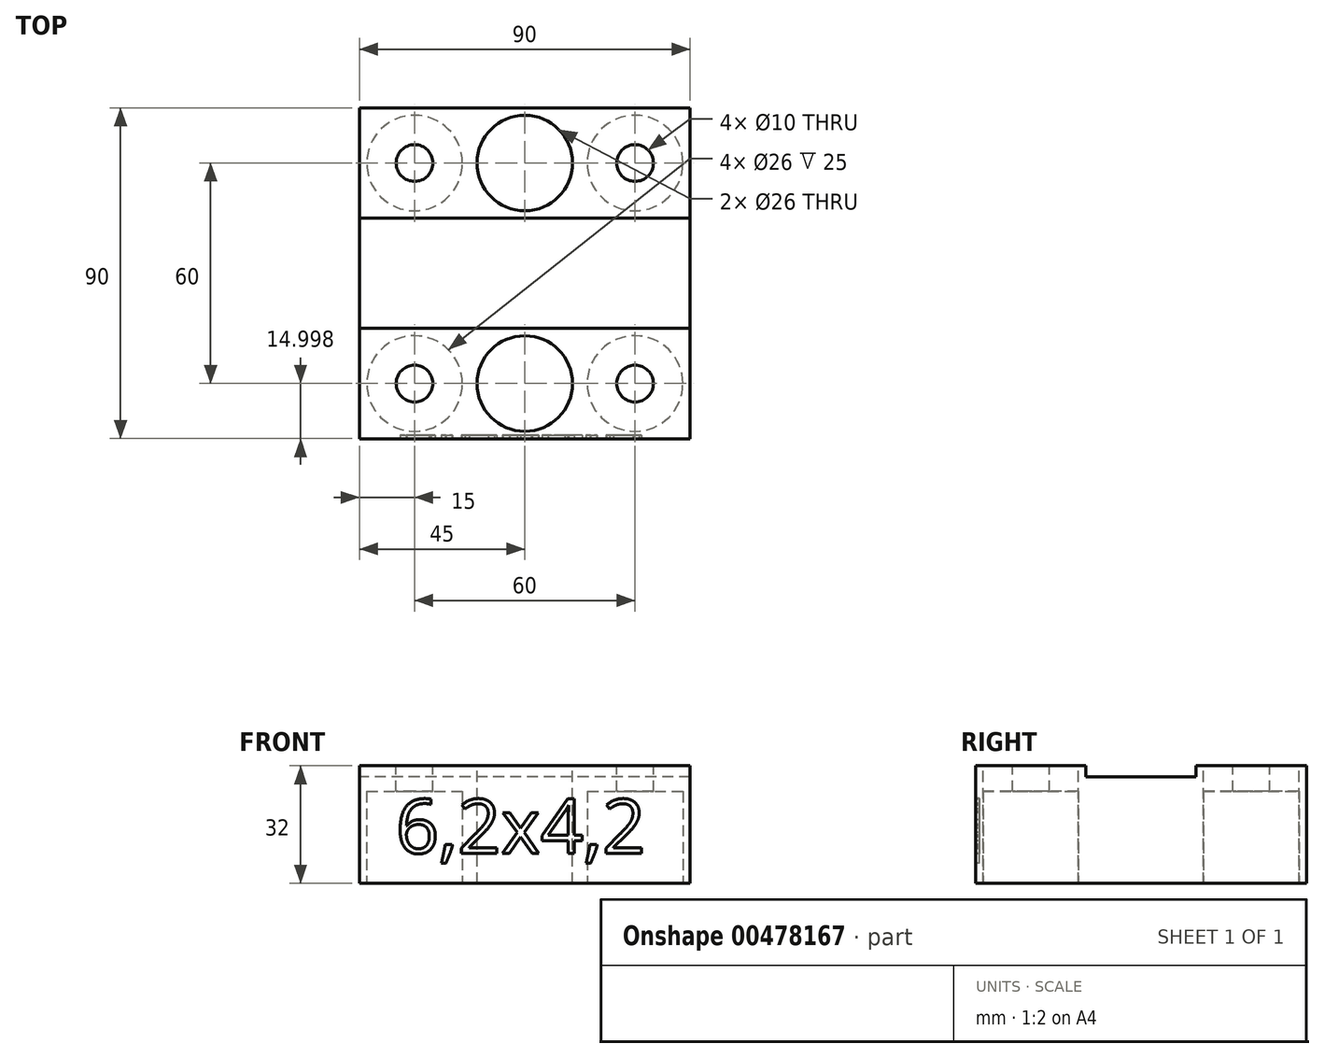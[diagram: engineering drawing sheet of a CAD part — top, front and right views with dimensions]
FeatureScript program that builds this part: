
annotation { "Feature Type Name" : "Feature", "Feature Type Description" : "" }
export const myFeature = defineFeature(function(context is Context, id is Id, definition is map)
    precondition{}
    {
        {
            var Q0;
            Q0=qCreatedBy(makeId("Right.planeOp"),FACE);
            var sketch = newSketch(context, id + "F0", { "sketchPlane" : qUnion([Q0])});
            skLineSegment(sketch, "E0", {"start": v(-46.9, -19.75) * mm, "end": v(43.1, -19.75) * mm});
            skLineSegment(sketch, "E1", {"start": v(43.1, -19.75) * mm, "end": v(43.1, 12.25) * mm});
            skLineSegment(sketch, "E2", {"start": v(43.1, 12.25) * mm, "end": v(13.1, 12.25) * mm});
            skLineSegment(sketch, "E3", {"start": v(13.1, 12.25) * mm, "end": v(13.1, 9.25) * mm});
            skLineSegment(sketch, "E4", {"start": v(13.1, 9.25) * mm, "end": v(-16.9, 9.25) * mm});
            skLineSegment(sketch, "E5", {"start": v(-16.9, 9.25) * mm, "end": v(-16.9, 12.25) * mm});
            skLineSegment(sketch, "E6", {"start": v(-16.9, 12.25) * mm, "end": v(-46.9, 12.25) * mm});
            skLineSegment(sketch, "E7", {"start": v(-46.9, 12.25) * mm, "end": v(-46.9, -19.75) * mm});
            skSolve(sketch);
        }
        {
            var Q0;
            Q0 = qSketchRegion(id + "F0", true);
            extrude(context, id + "F1", {"entities" : qUnion([Q0]), "depth" : 90 * mm});
        }
        {
            var Q0;
            Q0=makeQuery(id+"F1.opExtrude","SWEPT_FACE",FACE,{"disambiguationData":[OSD([sQuery(id+"F0.wireOp",EDGE,"E2")])]});
            var sketch = newSketch(context, id + "F2", { "sketchPlane" : qUnion([Q0])});
            skCircle(sketch, "E8", {"center": v(15, 28.1) * mm, "radius": 5 * mm});
            skCircle(sketch, "E9", {"center": v(75, 28.1) * mm, "radius": 5 * mm});
            skCircle(sketch, "E10", {"center": v(15, -31.9) * mm, "radius": 5 * mm});
            skCircle(sketch, "E11", {"center": v(75, -31.9) * mm, "radius": 5 * mm});
            skCircle(sketch, "E12", {"center": v(45, 28.1) * mm, "radius": 13 * mm});
            skCircle(sketch, "E13", {"center": v(45, -31.9) * mm, "radius": 13 * mm});
            skSolve(sketch);
        }
        {
            var Q0;
            Q0 = qSketchRegion(id + "F2", true);
            extrude(context, id + "F3", {"entities" : qUnion([Q0]), "operationType" : NewBodyOperationType.REMOVE, "endBound" : BoundingType.UP_TO_NEXT, "oppositeDirection" : true, "depth" : 25 * mm});
        }
        {
            var Q0;
            Q0=makeQuery(id+"F1.opExtrude","SWEPT_FACE",FACE,{"disambiguationData":[OSD([sQuery(id+"F0.wireOp",EDGE,"E0")])]});
            var sketch = newSketch(context, id + "F4", { "sketchPlane" : qUnion([Q0])});
            skCircle(sketch, "E14", {"center": v(15, 31.9) * mm, "radius": 13 * mm});
            skCircle(sketch, "E15", {"center": v(75, 31.9) * mm, "radius": 13 * mm});
            skCircle(sketch, "E16", {"center": v(15, -28.1) * mm, "radius": 13 * mm});
            skCircle(sketch, "E17", {"center": v(75, -28.1) * mm, "radius": 13 * mm});
            skSolve(sketch);
        }
        {
            var Q0;
            Q0 = qSketchRegion(id + "F4", true);
            extrude(context, id + "F5", {"entities" : qUnion([Q0]), "operationType" : NewBodyOperationType.REMOVE, "oppositeDirection" : true, "depth" : 25 * mm});
        }
        {
            var Q0;
            Q0=makeQuery(id+"F1.opExtrude","SWEPT_FACE",FACE,{"disambiguationData":[OSD([sQuery(id+"F0.wireOp",EDGE,"E7")])]});
            var sketch = newSketch(context, id + "F6", { "sketchPlane" : qUnion([Q0])});
            skText(sketch, "E18", { "text": "6,2x4,2", "fontName": "OpenSans-Regular.ttf"});
            const initialGuessF6  = {"E18": [0.0099, -0.01157, 1, 0, 0.01482]};
            skSetInitialGuess(sketch, initialGuessF6);
            skSolve(sketch);
        }
        {
            var Q0;
            Q0 = qSketchRegion(id + "F6", true);
            extrude(context, id + "F7", {"entities" : qUnion([Q0]), "operationType" : NewBodyOperationType.REMOVE, "oppositeDirection" : true, "depth" : 1 * mm});
        }
    });
